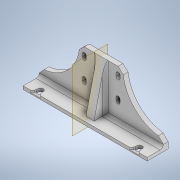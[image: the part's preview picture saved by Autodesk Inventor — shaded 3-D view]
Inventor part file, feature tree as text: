
AUTODESK INVENTOR PART (.ipt)
format: ipt  version: 2022.6 (Build 266554000, 554)  size: 254,976 bytes
history: native  units: mm
features: sketch x6, projected_geometry x5, extrude x4, chamfer x2, hole x1, plane x1, rib x1, fillet x1
ambient origin geometry x8: Origin, YZ Plane, XZ Plane, XY Plane, X Axis, Y Axis, Z Axis, Center Point
bodies: Solid1 (feature_tree)
feature tree (21):
  extrude  "Extrusion1"  Depth=2.0mm
  hole  "Hole1"  [1 undecoded]
  plane  "Work Plane1"
  rib  "Rib1"
  extrude  "Extrusion2"  Depth=3.0mm
  extrude  "Cam holes"  [1 undecoded]
  fillet  "Fillet1"  Radius=7.0mm
  extrude  "Extrusion4"  Depth=25.0mm
  chamfer  "Chamfer1"  [1 undecoded]
  chamfer  "Chamfer2"  Distance=21.0mm
  sketch  "Sketch1"  dims[d0=32.0mm d1=2.0mm]
  sketch  "Sketch2"  dims[d2=13.0mm d3=3.0mm]
  projected_geometry  "Projected Loop1"
  sketch  "Sketch3"  dims[d4=77.0mm d5=0.0mm d6=3.0mm]
  projected_geometry  "Projected Loop2"
  sketch  "Sketch4"  dims[d7=61.5mm]
  projected_geometry  "Projected Loop3"
  sketch  "Sketch5"  dims[d8=3.4mm d9=6.0mm d10=15.9mm d11=1.2mm d12=90.0deg d13=8.0mm d14=20.594885mm d15=-38.5mm d16=7.0mm]
  projected_geometry  "Projected Loop4"
  sketch  "Sketch6"  dims[d17=30.0mm d18=1.0mm d19=5.0mm d20=0.0mm d21=0.0mm d22=1.0mm d23=1.0mm d24=25.0mm d26=0.0mm d27=0.0mm d28=21.0mm d29=13.0mm d30=13.0mm d31=1.8mm d32=2.4mm d33=20.0mm d35=21.0mm d36=20.0mm d38=13.0mm d41=0.0mm d42=0.0mm d43=2.0mm d47=1.0mm d48=1.3mm d49=0.0mm d50=4.0mm d51=1.0mm d52=2.0mm d53=45.0deg d55=3.0mm d56=2.0mm d57=45.0deg]
  projected_geometry  "Projected Loop5"
note: 3 required parameter values undecoded (feature->parameter linkage not recoverable at this tier; creation-order binding heuristic only, values carry confidence <= 0.55)
